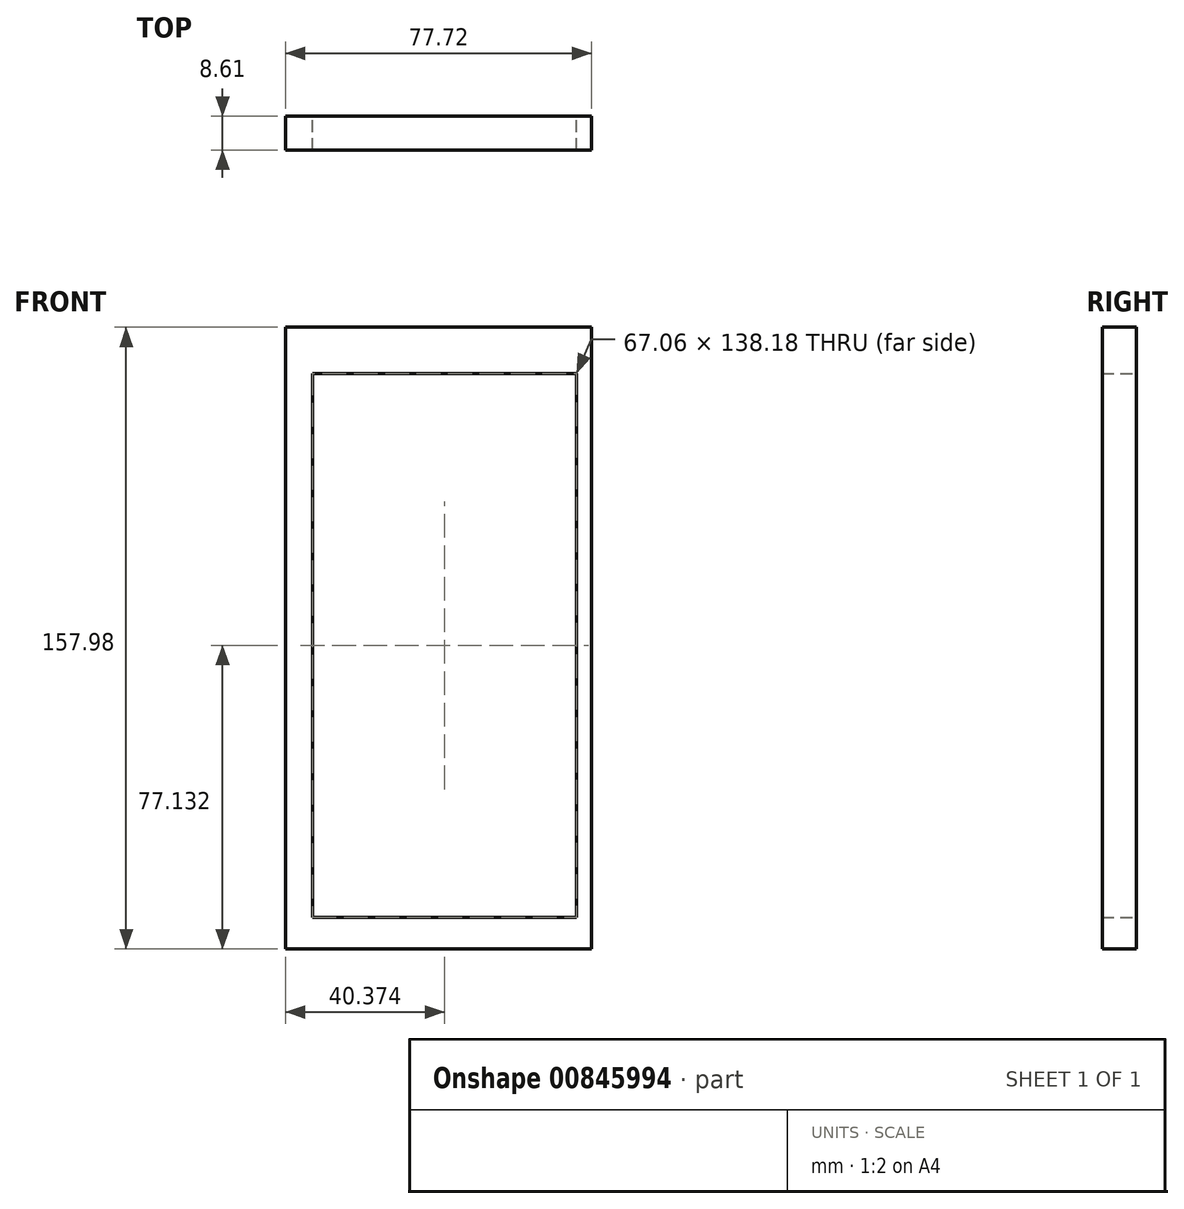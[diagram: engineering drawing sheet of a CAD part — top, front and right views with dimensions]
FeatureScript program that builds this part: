
annotation { "Feature Type Name" : "Feature", "Feature Type Description" : "" }
export const myFeature = defineFeature(function(context is Context, id is Id, definition is map)
    precondition{}
    {
        {
            var Q0;
            Q0=qCreatedBy(makeId("Front.planeOp"),FACE);
            var sketch = newSketch(context, id + "F0", { "sketchPlane" : qUnion([Q0])});
            skLineSegment(sketch, "E0", {"start": v(-38.43, 67.24) * mm, "end": v(-38.43, -70.94) * mm});
            skLineSegment(sketch, "E1", {"start": v(-38.43, -70.94) * mm, "end": v(28.62, -70.94) * mm});
            skLineSegment(sketch, "E2", {"start": v(28.62, -70.94) * mm, "end": v(28.62, 67.24) * mm});
            skLineSegment(sketch, "E3", {"start": v(28.62, 67.24) * mm, "end": v(-38.43, 67.24) * mm});
            skLineSegment(sketch, "E4", {"start": v(-38.43, 67.24) * mm, "end": v(28.62, 67.24) * mm});
            skLineSegment(sketch, "E5", {"start": v(-45.28, 79) * mm, "end": v(32.44, 79) * mm});
            skLineSegment(sketch, "E6", {"start": v(32.44, -78.98) * mm, "end": v(-45.28, -78.98) * mm});
            skPoint(sketch, "E7.start.orphan", {"position": v(32.44, -70.94) * mm});
            skPoint(sketch, "E8.start.orphan", {"position": v(-45.28, -70.94) * mm});
            skLineSegment(sketch, "E9", {"start": v(32.44, -78.98) * mm, "end": v(32.44, 79) * mm});
            skLineSegment(sketch, "E10", {"start": v(-45.28, 79) * mm, "end": v(-45.28, -78.98) * mm});
            skPoint(sketch, "E11.orphan", {"position": v(-45.28, 67.24) * mm});
            skPoint(sketch, "E12.orphan", {"position": v(32.44, 67.24) * mm});
            skSolve(sketch);
        }
        {
            var Q0;
            Q0=makeQuery(id+"F0.imprint","IMPRINT",FACE,{"disambiguationData":[TD([[makeQuery(id+"F0.imprint","IMPRINT",EDGE,{"derivedFrom":sQuery(id+"F0.wireOp",EDGE,"E1")}),-1.0]])]});
            extrude(context, id + "F1", {"entities" : qUnion([Q0]), "depth" : 8.6 * mm, "offsetDistance" : 25.4 * mm});
        }
    });
